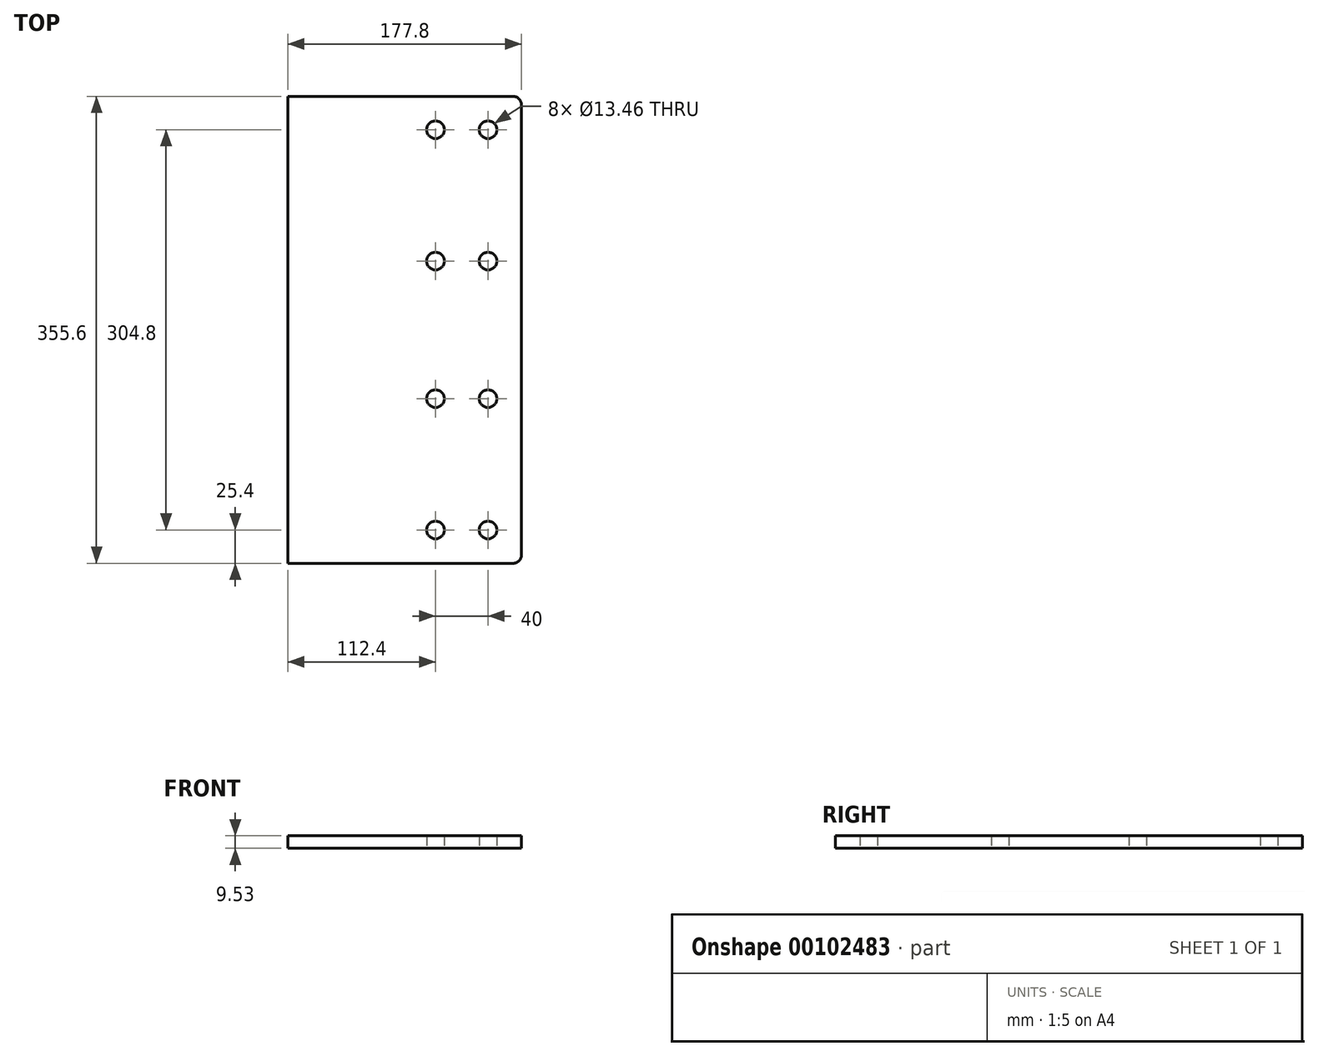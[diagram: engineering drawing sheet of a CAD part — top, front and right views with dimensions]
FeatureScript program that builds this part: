
annotation { "Feature Type Name" : "Feature", "Feature Type Description" : "" }
export const myFeature = defineFeature(function(context is Context, id is Id, definition is map)
    precondition{}
    {
        {
            var Q0;
            Q0=qCreatedBy(makeId("Top.planeOp"),FACE);
            var sketch = newSketch(context, id + "F0", { "sketchPlane" : qUnion([Q0])});
            skLineSegment(sketch, "E0", {"start": v(-88.9, -177.8) * mm, "end": v(82.55, -177.8) * mm});
            skLineSegment(sketch, "E1", {"start": v(88.9, -171.45) * mm, "end": v(88.9, 171.45) * mm});
            skLineSegment(sketch, "E2", {"start": v(82.55, 177.8) * mm, "end": v(-88.9, 177.8) * mm});
            skArc(sketch, "E3", {"start": v(88.9, 171.45) * mm, "mid": v(87.04, 175.94) * mm, "end": v(82.55, 177.8) * mm});
            skArc(sketch, "E4", {"start": v(82.55, -177.8) * mm, "mid": v(87.04, -175.94) * mm, "end": v(88.9, -171.45) * mm});
            skCircle(sketch, "E5", {"center": v(63.5, 52.4) * mm, "radius": 6.73 * mm});
            skCircle(sketch, "E6", {"center": v(23.5, 52.4) * mm, "radius": 6.73 * mm});
            skCircle(sketch, "E7", {"center": v(23.5, 152.4) * mm, "radius": 6.73 * mm});
            skCircle(sketch, "E8", {"center": v(63.5, 152.4) * mm, "radius": 6.73 * mm});
            skCircle(sketch, "E9", {"center": v(63.5, -152.4) * mm, "radius": 6.73 * mm});
            skCircle(sketch, "E10", {"center": v(23.5, -152.4) * mm, "radius": 6.73 * mm});
            skCircle(sketch, "E11", {"center": v(23.5, -52.4) * mm, "radius": 6.73 * mm});
            skCircle(sketch, "E12", {"center": v(63.5, -52.4) * mm, "radius": 6.73 * mm});
            skLineSegment(sketch, "E13", {"start": v(-88.9, 177.8) * mm, "end": v(-88.9, -177.8) * mm});
            skSolve(sketch);
        }
        {
            var Q0;
            Q0 = qSketchRegion(id + "F0", true);
            extrude(context, id + "F1", {"entities" : qUnion([Q0]), "depth" : 9.52 * mm});
        }
    });
